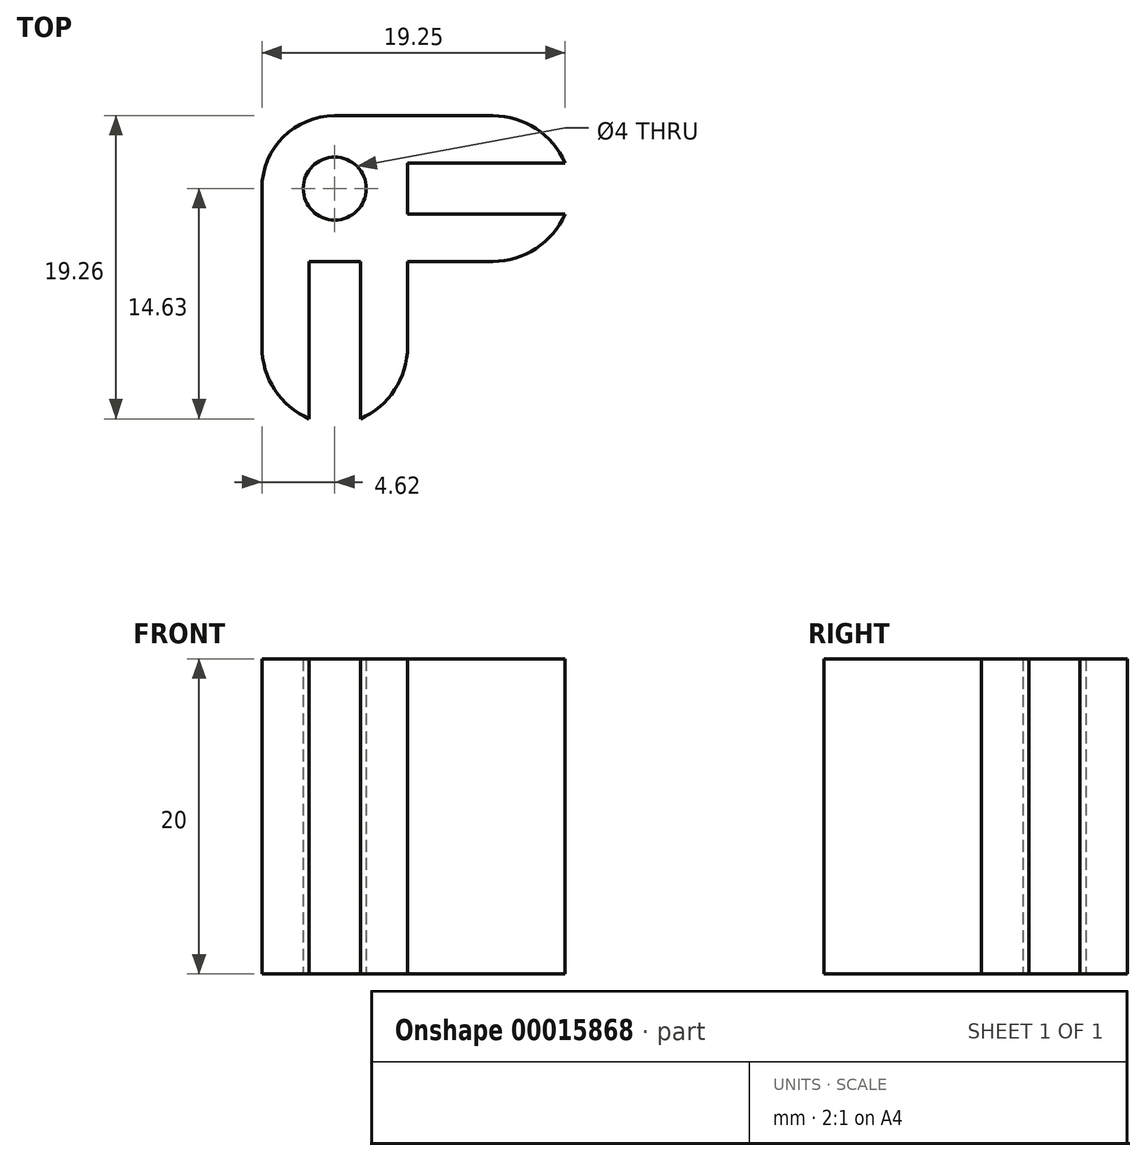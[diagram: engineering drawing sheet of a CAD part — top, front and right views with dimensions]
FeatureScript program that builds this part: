
annotation { "Feature Type Name" : "Feature", "Feature Type Description" : "" }
export const myFeature = defineFeature(function(context is Context, id is Id, definition is map)
    precondition{}
    {
        {
            var Q0;
            Q0=qCreatedBy(makeId("Top.planeOp"),FACE);
            var sketch = newSketch(context, id + "F0", { "sketchPlane" : qUnion([Q0])});
            skCircle(sketch, "E0", {"center": v(0, 0) * mm, "radius": 2 * mm});
            skLineSegment(sketch, "E1", {"start": v(0, 0) * mm, "end": v(0, 1.63) * mm});
            skCircle(sketch, "E2", {"center": v(0, 0) * mm, "radius": 4.62 * mm});
            skLineSegment(sketch, "E3", {"start": v(4.62, 0) * mm, "end": v(14.62, 0) * mm});
            skLineSegment(sketch, "E4", {"start": v(0, 4.62) * mm, "end": v(14.62, 4.62) * mm});
            skLineSegment(sketch, "E5", {"start": v(14.62, 4.62) * mm, "end": v(14.62, 1.63) * mm});
            skLineSegment(sketch, "E6", {"start": v(0, 0) * mm, "end": v(0, -1.63) * mm});
            skLineSegment(sketch, "E7", {"start": v(0, -1.63) * mm, "end": v(14.62, -1.63) * mm});
            skLineSegment(sketch, "E8", {"start": v(0, -4.62) * mm, "end": v(14.62, -4.62) * mm});
            skLineSegment(sketch, "E9", {"start": v(14.62, -4.62) * mm, "end": v(14.62, -1.63) * mm});
            skLineSegment(sketch, "E10", {"start": v(4.63, -1.63) * mm, "end": v(4.63, 1.63) * mm});
            skLineSegment(sketch, "E11", {"start": v(4.63, 1.63) * mm, "end": v(14.62, 1.63) * mm});
            skLineSegment(sketch, "E12.MirrorCS", {"start": v(4.62, 0) * mm, "end": v(4.62, -14.62) * mm});
            skLineSegment(sketch, "E13.MirrorCS", {"start": v(4.62, -14.62) * mm, "end": v(1.62, -14.62) * mm});
            skLineSegment(sketch, "E14.MirrorCS", {"start": v(1.63, 0) * mm, "end": v(1.62, -14.62) * mm});
            skLineSegment(sketch, "E15.MirrorCS", {"start": v(1.62, -4.63) * mm, "end": v(-1.63, -4.63) * mm});
            skLineSegment(sketch, "E16.MirrorCS", {"start": v(-1.63, -4.63) * mm, "end": v(-1.63, -14.62) * mm});
            skLineSegment(sketch, "E17.MirrorCS", {"start": v(-4.62, 0) * mm, "end": v(-4.63, -14.62) * mm});
            skLineSegment(sketch, "E18.MirrorCS", {"start": v(-4.63, -14.62) * mm, "end": v(-1.63, -14.62) * mm});
            skSolve(sketch);
        }
        {
            var Q0;
            Q0 = qSketchRegion(id + "F0", true);
            var Q1;
            {var subQ0=sQuery(id+"F0.wireOp",EDGE,"E14.MirrorCS");var subQ1=sQuery(id+"F0.wireOp",EDGE,"E2");var subQ2=makeQuery(id+"F0.imprint","INTERSECT",VERTEX,{"derivedFrom":[subQ1,subQ0]});Q1=makeQuery(id+"F0.imprint","IMPRINT",FACE,{"disambiguationData":[TD([[makeQuery(id+"F0.imprint","IMPRINT",EDGE,{"disambiguationData":[TD([[subQ2,-1.0]])],"derivedFrom":subQ1}),1.0]])]});}
            var Q2;
            {var subQ0=sQuery(id+"F0.wireOp",EDGE,"E7");var subQ1=sQuery(id+"F0.wireOp",EDGE,"E0");var subQ2=makeQuery(id+"F0.imprint","INTERSECT",VERTEX,{"derivedFrom":[subQ1,subQ0]});Q2=makeQuery(id+"F0.imprint","IMPRINT",FACE,{"disambiguationData":[TD([[makeQuery(id+"F0.imprint","IMPRINT",EDGE,{"disambiguationData":[TD([[subQ2,-1.0]])],"derivedFrom":subQ1}),-1.0]])]});}
            extrude(context, id + "F1", {"entities" : qUnion([Q0, Q1, Q2]), "depth" : 20 * mm});
        }
        {
            var Q0;
            Q0=makeQuery(id+"F1.opExtrude","SWEPT_EDGE",EDGE,{"disambiguationData":[OSD([sQuery(id+"F0.wireOp",EDGE,"E8"),sQuery(id+"F0.wireOp",EDGE,"E9")])]});
            var Q1;
            Q1=makeQuery(id+"F1.opExtrude","SWEPT_EDGE",EDGE,{"disambiguationData":[OSD([sQuery(id+"F0.wireOp",EDGE,"E4"),sQuery(id+"F0.wireOp",EDGE,"E5")])]});
            fillet(context, id + "F2", {"entities" : qUnion([Q0, Q1]), "radius" : 5 * mm, "tangentPropagation" : true, "allowEdgeOverflow" : false});
        }
        {
            var Q0;
            Q0=qCreatedBy(makeId("Top.planeOp"),FACE);
            var sketch = newSketch(context, id + "F3", { "sketchPlane" : qUnion([Q0])});
            skCircle(sketch, "E19.0", {"center": v(0, 0) * mm, "radius": 2 * mm});
            skSolve(sketch);
        }
        {
            var Q0;
            Q0=makeQuery(id+"F1.opExtrude","SWEPT_EDGE",EDGE,{"disambiguationData":[OSD([sQuery(id+"F0.wireOp",EDGE,"E17.MirrorCS"),sQuery(id+"F0.wireOp",EDGE,"E18.MirrorCS")])]});
            var Q1;
            Q1=makeQuery(id+"F1.opExtrude","SWEPT_EDGE",EDGE,{"disambiguationData":[OSD([sQuery(id+"F0.wireOp",EDGE,"E12.MirrorCS"),sQuery(id+"F0.wireOp",EDGE,"E13.MirrorCS")])]});
            fillet(context, id + "F4", {"entities" : qUnion([Q0, Q1]), "radius" : 5 * mm, "tangentPropagation" : true, "allowEdgeOverflow" : false});
        }
    });
